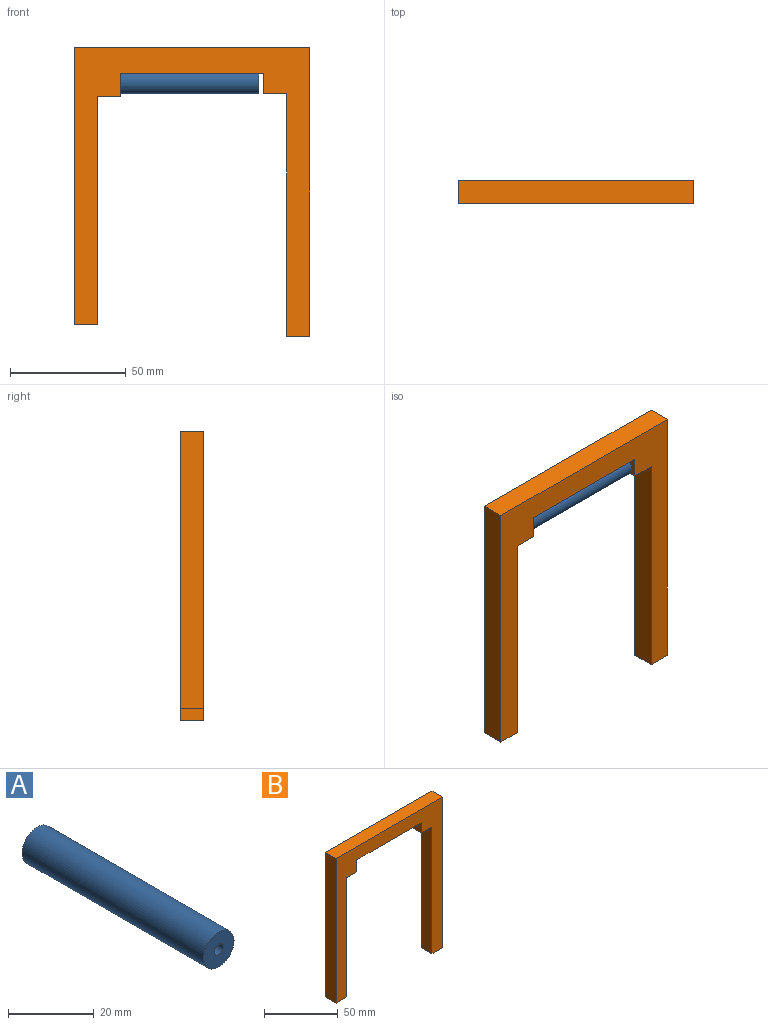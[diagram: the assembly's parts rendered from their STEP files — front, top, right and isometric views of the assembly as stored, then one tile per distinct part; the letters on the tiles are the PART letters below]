
ASSEMBLY  parts=2 mates=1
PART A: 4 faces, bbox 10x60x10 mm
  f0: cylinder r=1.5mm len=60mm, axis (0,-1,0), area 565.5mm2, adj f2,f3
  f1: cylinder r=5mm len=60mm, axis (0,-1,0), area 1885mm2, adj f2,f3
  f2: plane 10x10mm, normal (0,1,0), area 71.5mm2, adj f0,f1
  f3: plane 10x10mm, normal (0,-1,0), area 71.5mm2, adj f0,f1
PART B: 18 faces, bbox 102x10x125 mm
  f0: plane 125x10mm, normal (1,0,0), area 1250mm2, adj f1,f11,f12,f13
  f1: plane 102x10mm, normal (0,0,1), area 1020mm2, adj f0,f2,f12,f13
  f2: plane 120x10mm, normal (-1,0,0), area 1200mm2, adj f1,f3,f12,f13
  f3: plane 10x10mm, normal (0,0,-1), area 100mm2, adj f2,f4,f12,f13
  f4: plane 98.87x10mm, normal (1,0,0), area 988.7mm2, adj f3,f5,f12,f13
  f5: plane 10x10mm, normal (0,0,-1), area 100mm2, adj f4,f6,f12,f13
  f6: plane 10x10mm, normal (1,0,0), area 92.9mm2, adj f5,f7,f12,f13,f14
  f7: plane 62x10mm, normal (0,0,-1), area 620mm2, adj f6,f8,f12,f13
  f8: plane 10x8.87mm, normal (-1,0,0), area 81.6mm2, adj f7,f9,f12,f13,f16
  f9: plane 10x10mm, normal (0,0,-1), area 100mm2, adj f8,f10,f12,f13
  f10: plane 105x10mm, normal (-1,0,0), area 1050mm2, adj f9,f11,f12,f13
  f11: plane 10x10mm, normal (0,0,-1), area 100mm2, adj f0,f10,f12,f13
  f12: plane 125x102mm, normal (0,-1,0), area 3551.7mm2, adj f0,f1,f2,f3,f4,f5,f6,f7
  f13: plane 125x102mm, normal (0,1,0), area 3551.7mm2, adj f0,f1,f2,f3,f4,f5,f6,f7
  f14: cylinder r=1.5mm len=10mm, axis (1,0,0), area 94.2mm2, adj f6,f15
  f15: plane 3x3mm, normal (1,0,0), area 7.1mm2, adj f14
  f16: cylinder r=1.5mm len=10mm, axis (-1,0,0), area 94.2mm2, adj f8,f17
  f17: plane 3x3mm, normal (-1,0,0), area 7.1mm2, adj f16
PLACE A rot(axis=(0,0,1),90deg) t=(26.68,1.28,41.13)mm
PLACE B t=(-3.34,6.28,-14.23)mm
MATE fastened A.f0 <-> B.f14  axis (-1,0,0) through (-33.32,1.28,41.13)mm
